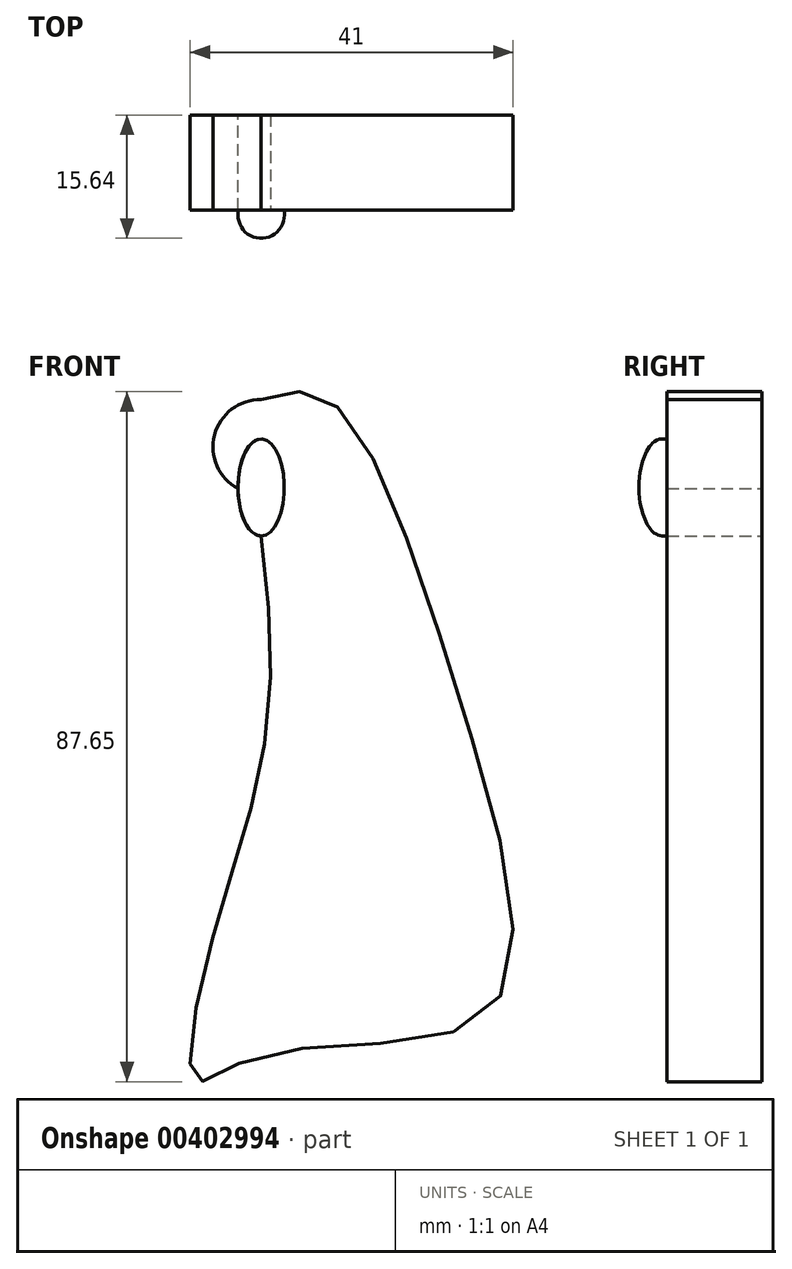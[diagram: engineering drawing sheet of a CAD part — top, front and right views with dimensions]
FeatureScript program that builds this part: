
annotation { "Feature Type Name" : "Feature", "Feature Type Description" : "" }
export const myFeature = defineFeature(function(context is Context, id is Id, definition is map)
    precondition{}
    {
        {
            var Q0;
            Q0=qCreatedBy(makeId("Front.planeOp"),FACE);
            var sketch = newSketch(context, id + "F0", { "sketchPlane" : qUnion([Q0])});
            skEllipse(sketch, "E0", {"center": v(-12.9, 41.37) * mm, "majorRadius": 6.15 * mm, "minorRadius": 2.94 * mm, "majorAxis": v(0, -1)});
            skArc(sketch, "E1", {"start": v(-12.9, 52.51) * mm, "mid": v(-18.82, 48.02) * mm, "end": v(-15.84, 41.2) * mm});
            skPoint(sketch, "E1.startSnap0", {"position": v(-12.9, 47.52) * mm});
            skFitSpline(sketch, "E2", {"points": [v(-12.9, 52.51) * mm, v(-4.43, 52.51) * mm, v(11.97, 15.6) * mm, v(15.83, -25.42) * mm, v(-12.9, -30.8) * mm, v(-21.27, -33.95) * mm, v(-19.55, -17.64) * mm, v(-12.62, 7.67) * mm, v(-12.9, 35.21) * mm], "startDerivative": vector(111.05, 34.28) * mm, "endDerivative": vector(-29.2, 213.88) * mm});
            skSolve(sketch);
        }
        {
            var Q0;
            {var subQ0=sQuery(id+"F0.wireOp",EDGE,"E0");var subQ1=makeQuery(id+"F0.imprint","INTERSECT",VERTEX,{"derivedFrom":[subQ0,sQuery(id+"F0.wireOp",EDGE,"E1")]});Q0=makeQuery(id+"F0.imprint","IMPRINT",FACE,{"disambiguationData":[TD([[makeQuery(id+"F0.imprint","IMPRINT",EDGE,{"disambiguationData":[TD([[subQ1,1.0]])],"derivedFrom":subQ0}),1.0]])]});}
            extrude(context, id + "F1", {"entities" : qUnion([Q0]), "depth" : 12.7 * mm});
        }
        {
            var Q0;
            {var subQ0=sQuery(id+"F0.wireOp",EDGE,"E1");Q0=makeQuery(id+"F0.imprint","IMPRINT",FACE,{"disambiguationData":[TD([[makeQuery(id+"F0.imprint","IMPRINT",EDGE,{"derivedFrom":subQ0}),1.0]])]});}
            extrude(context, id + "F2", {"entities" : qUnion([Q0]), "operationType" : NewBodyOperationType.ADD, "depth" : 12.06 * mm});
        }
        {
            var Q0;
            Q0=makeQuery(id+"F1.opExtrude","CAP_FACE",FACE,{"disambiguationData":[OSD([sQuery(id+"F0.wireOp",EDGE,"E0")])],"isStart":false});
            var sketch = newSketch(context, id + "F3", { "sketchPlane" : qUnion([Q0])});
            skLineSegment(sketch, "E3", {"start": v(-12.9, 47.52) * mm, "end": v(-12.9, 35.21) * mm});
            skSolve(sketch);
        }
        {
            var Q0;
            {var subQ0=sQuery(id+"F3.wireOp",EDGE,"E3");Q0=makeQuery(id+"F3.imprint","IMPRINT",FACE,{"disambiguationData":[TD([[makeQuery(id+"F3.imprint","IMPRINT",EDGE,{"derivedFrom":subQ0}),-1.0]])]});}
            var Q1;
            Q1=sQuery(id+"F3.wireOp",EDGE,"E3");
            revolve(context, id + "F4", {"operationType" : NewBodyOperationType.ADD, "entities" : qUnion([Q0]), "axis" : qUnion([Q1]), "revolveType" : RevolveType.FULL});
        }
    });
